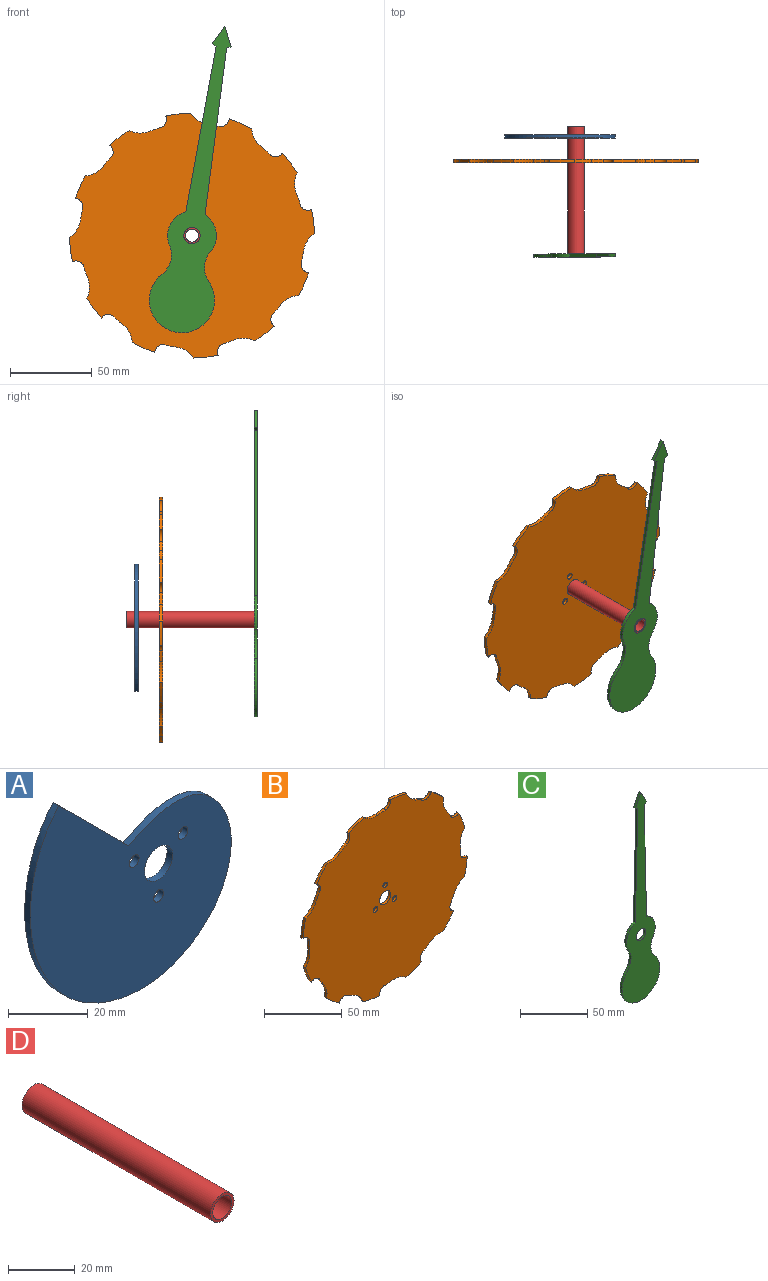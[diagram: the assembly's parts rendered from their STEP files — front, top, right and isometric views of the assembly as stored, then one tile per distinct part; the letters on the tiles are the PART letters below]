
ASSEMBLY  parts=4 mates=5
PART A: 8 faces, bbox 72.9x2x71.7 mm
  f0: extruded ~71.13x70.76mm, area 387.9mm2, adj f1,f3,f4
  f1: plane 24.75x24.75mm, normal (0.71,0,0.71), area 70mm2, adj f0,f3,f4
  f2: cylinder r=5mm len=10mm, axis (0,1,0), area 62.8mm2, adj f3,f4
  f3: plane 72.86x71.69mm, normal (0,-1,0), area 3161.4mm2, adj f0,f1,f2,f5,f6,f7
  f4: plane 72.86x71.69mm, normal (0,1,0), area 3161.4mm2, adj f0,f1,f2,f5,f6,f7
  f5: cylinder r=1.75mm len=3.5mm, axis (0,-1,0), area 22mm2, adj f3,f4
  f6: cylinder r=1.75mm len=3.5mm, axis (0,-1,0), area 22mm2, adj f3,f4
  f7: cylinder r=1.75mm len=3.5mm, axis (0,-1,0), area 22mm2, adj f3,f4
PART B: 54 faces, bbox 149.7x2x149.7 mm
  f0: cylinder r=75mm len=11.65mm, axis (0,1,0), area 30.3mm2, adj f13,f14,f47,f48
  f1: cylinder r=75mm len=14.9mm, axis (0,1,0), area 30.3mm2, adj f13,f14,f44,f45
  f2: cylinder r=75mm len=14.16mm, axis (0,1,0), area 30.3mm2, adj f13,f14,f41,f42
  f3: cylinder r=75mm len=11.65mm, axis (0,1,0), area 30.3mm2, adj f13,f14,f38,f39
  f4: cylinder r=75mm len=14.9mm, axis (0,1,0), area 30.3mm2, adj f13,f14,f35,f36
  f5: cylinder r=75mm len=14.16mm, axis (0,1,0), area 30.3mm2, adj f13,f14,f32,f33
  f6: cylinder r=75mm len=11.65mm, axis (0,1,0), area 30.3mm2, adj f13,f14,f29,f30
  f7: cylinder r=75mm len=14.9mm, axis (0,1,0), area 30.3mm2, adj f13,f14,f17,f27
  f8: cylinder r=75mm len=14.16mm, axis (0,1,0), area 30.3mm2, adj f13,f14,f24,f50
  f9: cylinder r=75mm len=14.9mm, axis (0,1,0), area 30.3mm2, adj f13,f14,f21,f26
  f10: cylinder r=75mm len=11.65mm, axis (0,1,0), area 30.3mm2, adj f13,f14,f18,f23
  f11: cylinder r=5mm len=10mm, axis (0,1,0), area 62.8mm2, adj f13,f14
  f12: cylinder r=75mm len=14.16mm, axis (0,1,0), area 30.3mm2, adj f13,f14,f15,f20
  f13: plane 149.68x149.68mm, normal (0,-1,0), area 16158.8mm2, adj f0,f1,f2,f3,f4,f5,f6,f7
  f14: plane 149.68x149.68mm, normal (0,1,0), area 16158.8mm2, adj f0,f1,f2,f3,f4,f5,f6,f7
  f15: cylinder r=15mm len=11.78mm, axis (0,-1,0), area 25.6mm2, adj f12,f13,f14,f16
  f16: cylinder r=69mm len=7.21mm, axis (0,-1,0), area 14.5mm2, adj f13,f14,f15,f17
  f17: cylinder r=5mm len=5.84mm, axis (0,-1,0), area 17.4mm2, adj f7,f13,f14,f16
  f18: cylinder r=15mm len=12.17mm, axis (0,-1,0), area 25.6mm2, adj f10,f13,f14,f19
  f19: cylinder r=69mm len=6.06mm, axis (0,-1,0), area 14.5mm2, adj f13,f14,f18,f20
  f20: cylinder r=5mm len=7.52mm, axis (0,-1,0), area 17.4mm2, adj f12,f13,f14,f19
  f21: cylinder r=15mm len=9.3mm, axis (0,-1,0), area 25.6mm2, adj f9,f13,f14,f22
  f22: cylinder r=69mm len=6.44mm, axis (0,-1,0), area 14.5mm2, adj f13,f14,f21,f23
  f23: cylinder r=5mm len=7.19mm, axis (0,-1,0), area 17.4mm2, adj f10,f13,f14,f22
  f24: cylinder r=15mm len=11.78mm, axis (0,-1,0), area 25.6mm2, adj f8,f13,f14,f25
  f25: cylinder r=69mm len=7.21mm, axis (0,-1,0), area 14.5mm2, adj f13,f14,f24,f26
  f26: cylinder r=5mm len=5.84mm, axis (0,-1,0), area 17.4mm2, adj f9,f13,f14,f25
  f27: cylinder r=15mm len=9.3mm, axis (0,-1,0), area 25.6mm2, adj f7,f13,f14,f28
  f28: cylinder r=69mm len=6.44mm, axis (0,-1,0), area 14.5mm2, adj f13,f14,f27,f29
  f29: cylinder r=5mm len=7.19mm, axis (0,-1,0), area 17.4mm2, adj f6,f13,f14,f28
  f30: cylinder r=15mm len=12.17mm, axis (0,-1,0), area 25.6mm2, adj f6,f13,f14,f31
  f31: cylinder r=69mm len=6.06mm, axis (0,-1,0), area 14.5mm2, adj f13,f14,f30,f32
  f32: cylinder r=5mm len=7.52mm, axis (0,-1,0), area 17.4mm2, adj f5,f13,f14,f31
  f33: cylinder r=15mm len=11.78mm, axis (0,-1,0), area 25.6mm2, adj f5,f13,f14,f34
  f34: cylinder r=69mm len=7.21mm, axis (0,-1,0), area 14.5mm2, adj f13,f14,f33,f35
  f35: cylinder r=5mm len=5.84mm, axis (0,-1,0), area 17.4mm2, adj f4,f13,f14,f34
  f36: cylinder r=15mm len=9.3mm, axis (0,-1,0), area 25.6mm2, adj f4,f13,f14,f37
  f37: cylinder r=69mm len=6.44mm, axis (0,-1,0), area 14.5mm2, adj f13,f14,f36,f38
  f38: cylinder r=5mm len=7.19mm, axis (0,-1,0), area 17.4mm2, adj f3,f13,f14,f37
  f39: cylinder r=15mm len=12.17mm, axis (0,-1,0), area 25.6mm2, adj f3,f13,f14,f40
  f40: cylinder r=69mm len=6.06mm, axis (0,-1,0), area 14.5mm2, adj f13,f14,f39,f41
  f41: cylinder r=5mm len=7.52mm, axis (0,-1,0), area 17.4mm2, adj f2,f13,f14,f40
  f42: cylinder r=15mm len=11.78mm, axis (0,-1,0), area 25.6mm2, adj f2,f13,f14,f43
  f43: cylinder r=69mm len=7.21mm, axis (0,-1,0), area 14.5mm2, adj f13,f14,f42,f44
  f44: cylinder r=5mm len=5.84mm, axis (0,-1,0), area 17.4mm2, adj f1,f13,f14,f43
  f45: cylinder r=15mm len=9.3mm, axis (0,-1,0), area 25.6mm2, adj f1,f13,f14,f46
  f46: cylinder r=69mm len=6.44mm, axis (0,-1,0), area 14.5mm2, adj f13,f14,f45,f47
  f47: cylinder r=5mm len=7.19mm, axis (0,-1,0), area 17.4mm2, adj f0,f13,f14,f46
  f48: cylinder r=15mm len=12.17mm, axis (0,-1,0), area 25.6mm2, adj f0,f13,f14,f49
  f49: cylinder r=69mm len=6.06mm, axis (0,-1,0), area 14.5mm2, adj f13,f14,f48,f50
  f50: cylinder r=5mm len=7.52mm, axis (0,-1,0), area 17.4mm2, adj f8,f13,f14,f49
  f51: cylinder r=2mm len=4mm, axis (0,-1,0), area 25.1mm2, adj f13,f14
  f52: cylinder r=2mm len=4mm, axis (0,-1,0), area 25.1mm2, adj f13,f14
  f53: cylinder r=2mm len=4mm, axis (0,-1,0), area 25.1mm2, adj f13,f14
PART C: 14 faces, bbox 40x2x190 mm
  f0: plane 2.69x2mm, normal (0.45,0,-0.89), area 6mm2, adj f1,f10,f12,f13
  f1: plane 11.91x5.95mm, normal (0.89,0,0.45), area 26.6mm2, adj f0,f2,f12,f13
  f2: plane 11.91x5.95mm, normal (-0.89,0,0.45), area 26.6mm2, adj f1,f3,f12,f13
  f3: plane 2.69x2mm, normal (-0.45,0,-0.89), area 6mm2, adj f2,f4,f12,f13
  f4: plane 102.98x2.69mm, normal (-1,0,0.03), area 206mm2, adj f3,f5,f12,f13
  f5: cylinder r=15mm len=21.74mm, axis (0,1,0), area 51.7mm2, adj f4,f6,f12,f13
  f6: cylinder r=15mm len=18.28mm, axis (0,1,0), area 39.5mm2, adj f5,f7,f12,f13
  f7: cylinder r=20mm len=40mm, axis (0,1,0), area 186.3mm2, adj f6,f8,f12,f13
  f8: cylinder r=15mm len=18.28mm, axis (0,1,0), area 39.5mm2, adj f7,f9,f12,f13
  f9: cylinder r=15mm len=21.74mm, axis (0,1,0), area 51.7mm2, adj f8,f10,f12,f13
  f10: plane 102.98x2.69mm, normal (1,0,0.03), area 206mm2, adj f0,f9,f12,f13
  f11: cylinder r=5mm len=10mm, axis (0,1,0), area 62.8mm2, adj f12,f13
  f12: plane 190x40mm, normal (0,-1,0), area 3073.4mm2, adj f0,f1,f2,f3,f4,f5,f6,f7
  f13: plane 190x40mm, normal (0,1,0), area 3073.4mm2, adj f0,f1,f2,f3,f4,f5,f6,f7
PART D: 4 faces, bbox 10x80x10 mm
  f0: cylinder r=4mm len=80mm, axis (0,1,0), area 2010.6mm2, adj f2,f3
  f1: cylinder r=5mm len=80mm, axis (0,1,0), area 2513.3mm2, adj f2,f3
  f2: plane 10x10mm, normal (0,-1,0), area 28.3mm2, adj f0,f1
  f3: plane 10x10mm, normal (0,1,0), area 28.3mm2, adj f0,f1
PLACE A rot(axis=(0.99,0,0.14),180deg) t=(131.43,-10.22,-14.63)mm
PLACE B rot(axis=(0,-1,0),16.1deg) t=(131.43,-23.22,-14.63)mm
PLACE C rot(axis=(0,1,0),8.9deg) t=(131.43,-81.22,-14.63)mm
PLACE D t=(131.43,-3.22,-14.63)mm
MATE slider B.f52 <-> A.f6  axis (0,1,0) through (141.14,-23.22,-17.03)mm
MATE revolute D.f1 <-> A.f2  axis (0,1,0) through (131.43,-3.22,-14.63)mm
MATE revolute D.f1 <-> B.f11  axis (0,1,0) through (131.43,-3.22,-14.63)mm
MATE cylindrical D.f1 <-> C.f11  axis (0,1,0) through (131.43,-43.22,-14.63)mm
MATE planar D.f1 <-> C.f12  axis (0,-1,0) through (131.43,-83.22,-14.63)mm
